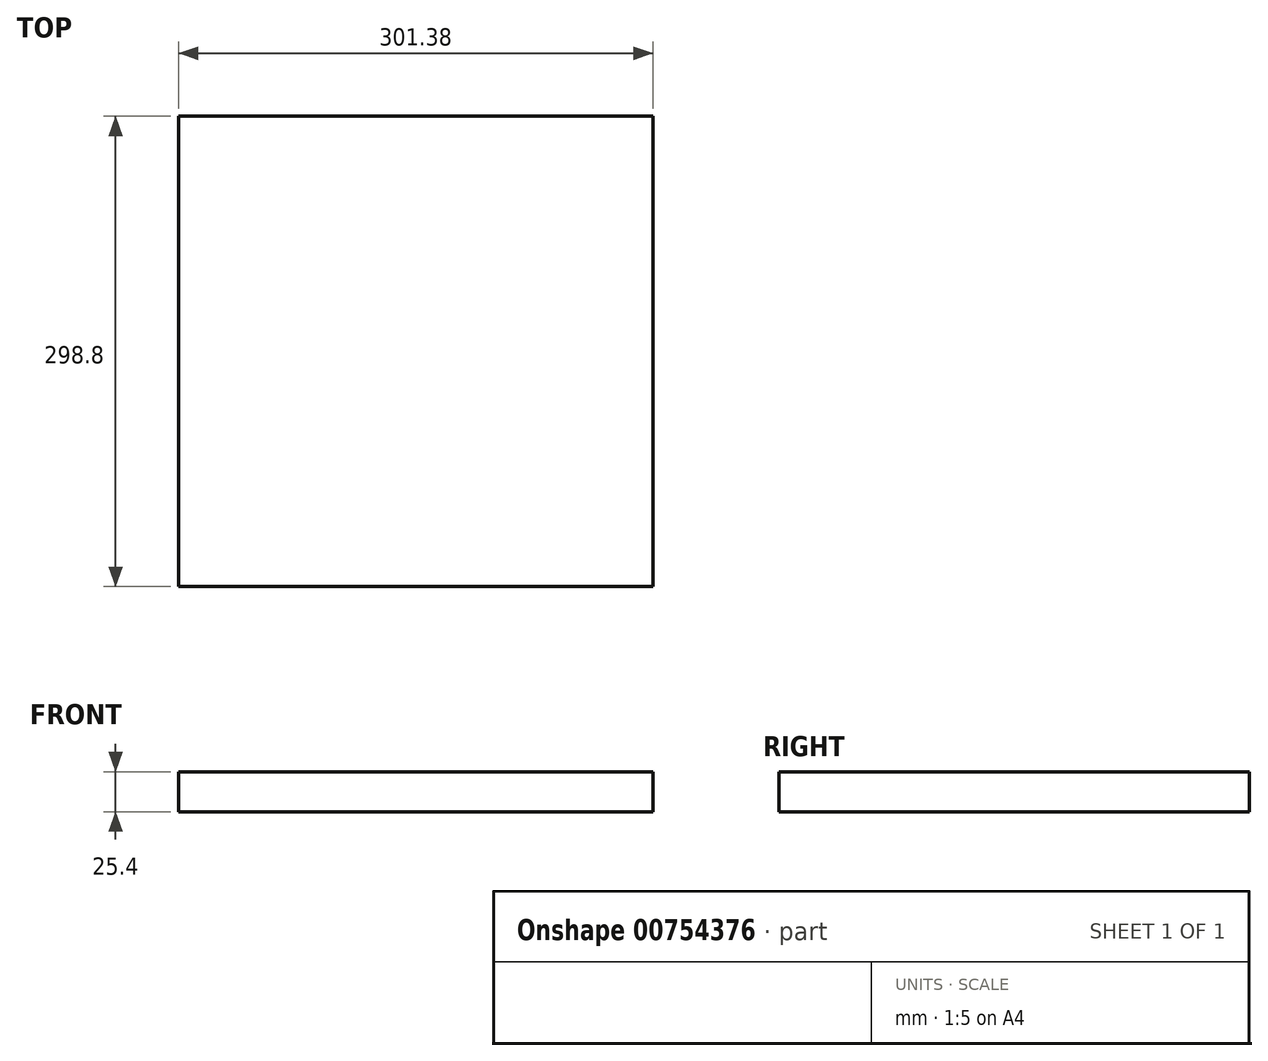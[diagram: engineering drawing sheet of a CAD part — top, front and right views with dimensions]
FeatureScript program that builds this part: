
annotation { "Feature Type Name" : "Feature", "Feature Type Description" : "" }
export const myFeature = defineFeature(function(context is Context, id is Id, definition is map)
    precondition{}
    {
        {
            var Q0;
            Q0=qCreatedBy(makeId("Top.planeOp"),FACE);
            var sketch = newSketch(context, id + "F0", { "sketchPlane" : qUnion([Q0])});
            skLineSegment(sketch, "E0.bottom", {"start": v(-150.7, 149.4) * mm, "end": v(150.7, 149.4) * mm});
            skLineSegment(sketch, "E0.top", {"start": v(-150.7, -149.4) * mm, "end": v(150.7, -149.4) * mm});
            skLineSegment(sketch, "E0.left", {"start": v(-150.7, 149.4) * mm, "end": v(-150.7, -149.4) * mm});
            skLineSegment(sketch, "E0.right", {"start": v(150.7, 149.4) * mm, "end": v(150.7, -149.4) * mm});
            skPoint(sketch, "E0.middle", {"position": v(0, 0) * mm});
            skSolve(sketch);
        }
        {
            var Q0;
            Q0 = qSketchRegion(id + "F0", true);
            extrude(context, id + "F1", {"entities" : qUnion([Q0]), "depth" : 25.4 * mm, "offsetDistance" : 25.4 * mm});
        }
    });
